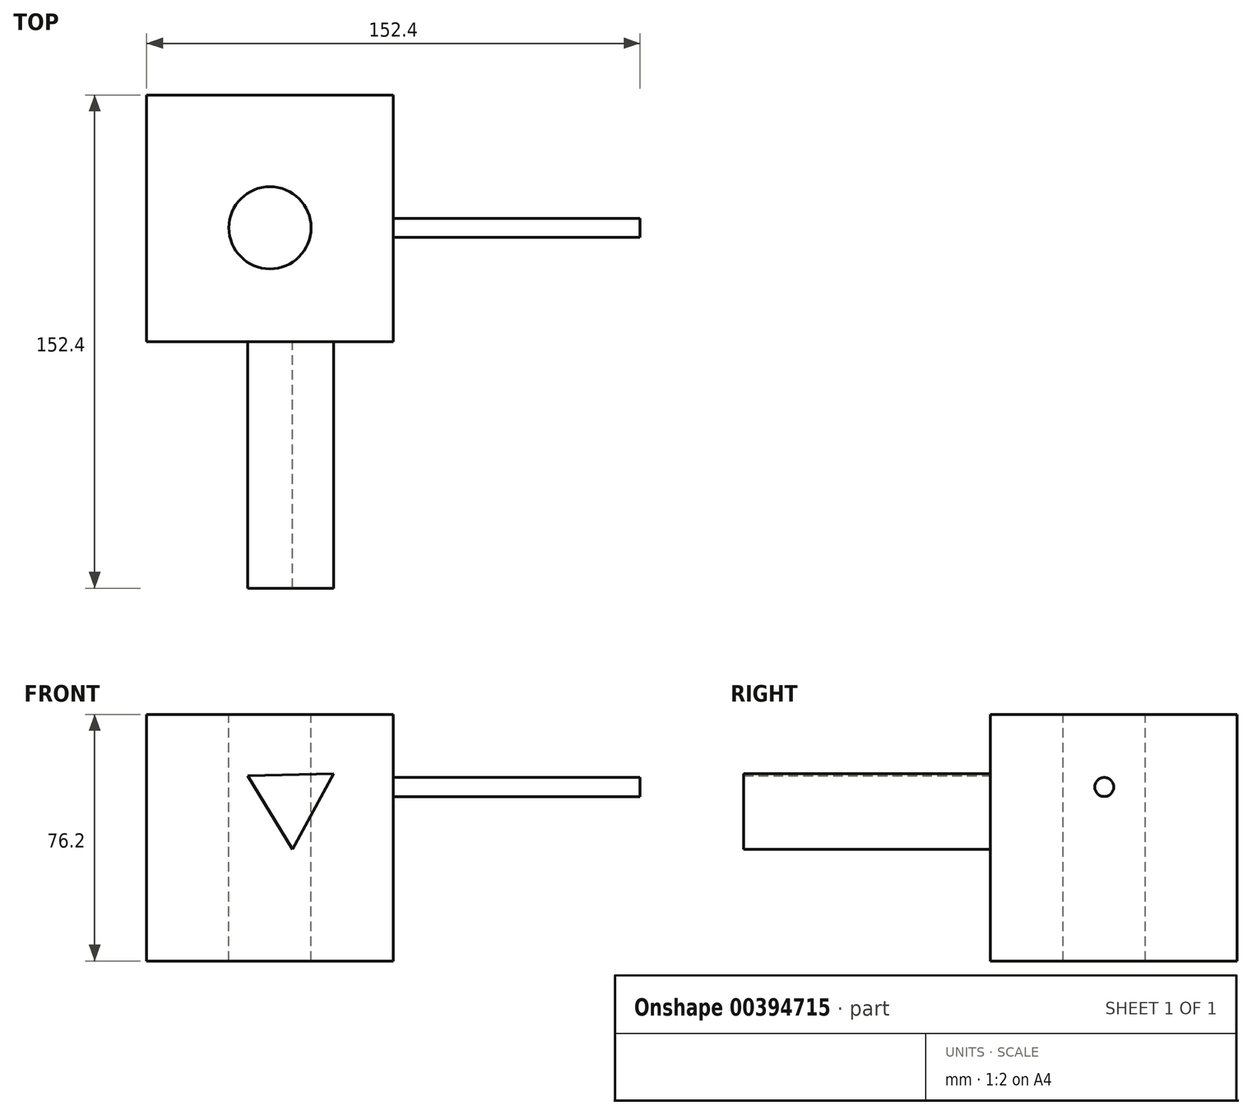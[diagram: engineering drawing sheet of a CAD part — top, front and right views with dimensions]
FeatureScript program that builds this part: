
annotation { "Feature Type Name" : "Feature", "Feature Type Description" : "" }
export const myFeature = defineFeature(function(context is Context, id is Id, definition is map)
    precondition{}
    {
        {
            var Q0;
            Q0=qCreatedBy(makeId("Right.planeOp"),FACE);
            var sketch = newSketch(context, id + "F0", { "sketchPlane" : qUnion([Q0])});
            skLineSegment(sketch, "E0.bottom", {"start": v(-35.16, 51.73) * mm, "end": v(41.04, 51.73) * mm});
            skLineSegment(sketch, "E0.top", {"start": v(-35.16, -24.47) * mm, "end": v(41.04, -24.47) * mm});
            skLineSegment(sketch, "E0.left", {"start": v(-35.16, 51.73) * mm, "end": v(-35.16, -24.47) * mm});
            skLineSegment(sketch, "E0.right", {"start": v(41.04, 51.73) * mm, "end": v(41.04, -24.47) * mm});
            skSolve(sketch);
        }
        {
            var Q0;
            Q0=makeQuery(id+"F0.imprint","IMPRINT",FACE,{"disambiguationData":[TD([[makeQuery(id+"F0.imprint","IMPRINT",EDGE,{"derivedFrom":sQuery(id+"F0.wireOp",EDGE,"E0.bottom")}),-1.0]])]});
            extrude(context, id + "F1", {"entities" : qUnion([Q0]), "depth" : 76.2 * mm});
        }
        {
            var Q0;
            Q0=makeQuery(id+"F1.opExtrude","SWEPT_FACE",FACE,{"disambiguationData":[OSD([sQuery(id+"F0.wireOp",EDGE,"E0.bottom")])]});
            var sketch = newSketch(context, id + "F2", { "sketchPlane" : qUnion([Q0])});
            skPoint(sketch, "E1", {"position": v(38.1, 0) * mm});
            skSolve(sketch);
        }
        {
            var Q0;
            Q0=sQuery(id+"F2.wireOp",VERTEX,"E1");
            var Q1;
            Q1=makeQuery(id+"F1.opExtrude","SWEPT_BODY",BODY,{"disambiguationData":[OSD([sQuery(id+"F0.wireOp",EDGE,"E0.bottom"),sQuery(id+"F0.wireOp",EDGE,"E0.top"),sQuery(id+"F0.wireOp",EDGE,"E0.left"),sQuery(id+"F0.wireOp",EDGE,"E0.right")])]});
            hole(context, id + "F3", {"style" : HoleStyle.SIMPLE, "endStyle" : HoleEndStyle.THROUGH, "holeDiameter" : 25.4 * mm, "isTappedThrough" : true, "tappedDepth" : 12.7 * mm, "tapClearance" : 3, "locations" : qUnion([Q0]), "scope" : qUnion([Q1])});
        }
        {
            var Q0;
            Q0=makeQuery(id+"F1.opExtrude","SWEPT_FACE",FACE,{"disambiguationData":[OSD([sQuery(id+"F0.wireOp",EDGE,"E0.left")])]});
            var sketch = newSketch(context, id + "F4", { "sketchPlane" : qUnion([Q0])});
            skCircle(sketch, "E2.cCircle", {"center": v(44.65, 25.4) * mm, "radius": 7.68 * mm, "construction": true});
            skLineSegment(sketch, "E2.0", {"start": v(45.05, 10.04) * mm, "end": v(31.15, 32.73) * mm});
            skLineSegment(sketch, "E2.1", {"start": v(31.15, 32.73) * mm, "end": v(57.75, 33.43) * mm});
            skLineSegment(sketch, "E2.2", {"start": v(57.75, 33.43) * mm, "end": v(45.05, 10.04) * mm});
            skPoint(sketch, "E2.0.midPoint", {"position": v(38.1, 21.38) * mm});
            skSolve(sketch);
        }
        {
            var Q0;
            Q0=makeQuery(id+"F4.imprint","IMPRINT",FACE,{"disambiguationData":[TD([[makeQuery(id+"F4.imprint","IMPRINT",EDGE,{"derivedFrom":sQuery(id+"F4.wireOp",EDGE,"E2.0")}),-1.0]])]});
            extrude(context, id + "F5", {"entities" : qUnion([Q0]), "operationType" : NewBodyOperationType.ADD, "depth" : 76.2 * mm});
        }
        {
            var Q0;
            Q0=makeQuery(id+"F1.opExtrude","CAP_FACE",FACE,{"disambiguationData":[OSD([sQuery(id+"F0.wireOp",EDGE,"E0.bottom"),sQuery(id+"F0.wireOp",EDGE,"E0.top"),sQuery(id+"F0.wireOp",EDGE,"E0.left"),sQuery(id+"F0.wireOp",EDGE,"E0.right")])],"isStart":false});
            var sketch = newSketch(context, id + "F6", { "sketchPlane" : qUnion([Q0])});
            skCircle(sketch, "E3", {"center": v(0, 29.27) * mm, "radius": 2.94 * mm});
            skSolve(sketch);
        }
        {
            var Q0;
            Q0=makeQuery(id+"F6.imprint","IMPRINT",FACE,{"disambiguationData":[TD([[makeQuery(id+"F6.imprint","IMPRINT",EDGE,{"derivedFrom":sQuery(id+"F6.wireOp",EDGE,"E3")}),1.0]])]});
            extrude(context, id + "F7", {"entities" : qUnion([Q0]), "operationType" : NewBodyOperationType.ADD, "depth" : 76.2 * mm});
        }
    });
